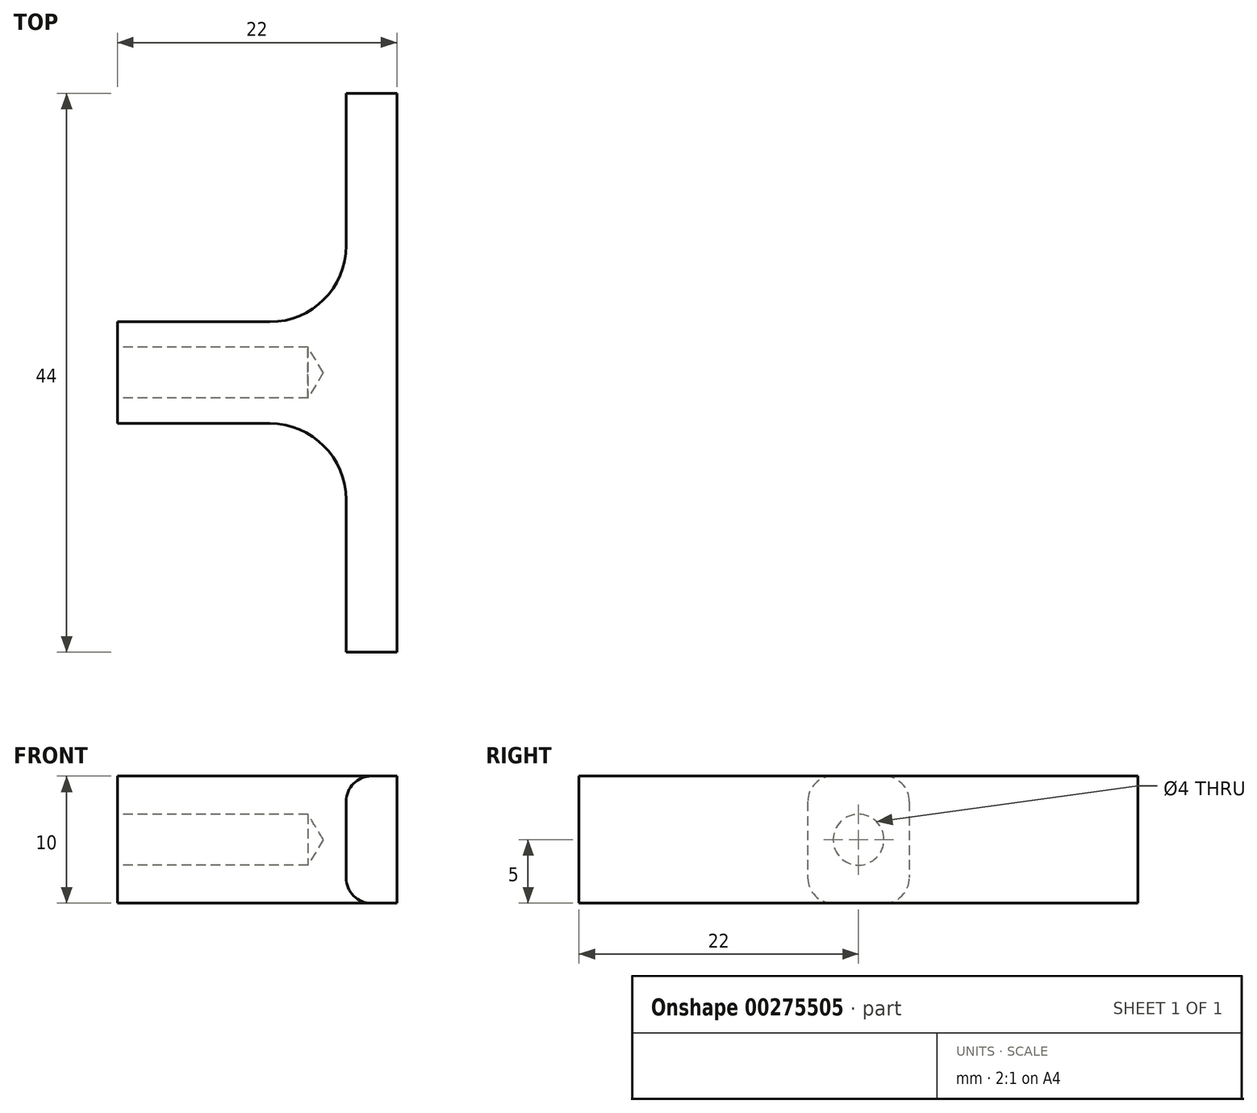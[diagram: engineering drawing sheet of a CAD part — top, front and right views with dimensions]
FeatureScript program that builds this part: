
annotation { "Feature Type Name" : "Feature", "Feature Type Description" : "" }
export const myFeature = defineFeature(function(context is Context, id is Id, definition is map)
    precondition{}
    {
        {
            var Q0;
            Q0=qCreatedBy(makeId("Top.planeOp"),FACE);
            var sketch = newSketch(context, id + "F0", { "sketchPlane" : qUnion([Q0])});
            skLineSegment(sketch, "E0", {"start": v(0, 0) * mm, "end": v(0, -22) * mm});
            skLineSegment(sketch, "E1", {"start": v(0, -22) * mm, "end": v(-4, -22) * mm});
            skLineSegment(sketch, "E2", {"start": v(-4, -22) * mm, "end": v(-4, -10) * mm});
            skLineSegment(sketch, "E3", {"start": v(-10, -4) * mm, "end": v(-22, -4) * mm});
            skLineSegment(sketch, "E4", {"start": v(-22, -4) * mm, "end": v(-22, 0) * mm});
            skPoint(sketch, "E5.visualSharp", {"position": v(-4, -4) * mm});
            skArc(sketch, "E5.filletArc", {"start": v(-4, -10) * mm, "mid": v(-5.76, -5.76) * mm, "end": v(-10, -4) * mm});
            skLineSegment(sketch, "E6.MirrorCS", {"start": v(-22, 4) * mm, "end": v(-22, 0) * mm});
            skLineSegment(sketch, "E7.MirrorCS", {"start": v(-10, 4) * mm, "end": v(-22, 4) * mm});
            skArc(sketch, "E8.MirrorCS", {"start": v(-4, 10) * mm, "mid": v(-5.76, 5.76) * mm, "end": v(-10, 4) * mm});
            skLineSegment(sketch, "E9.MirrorCS", {"start": v(-4, 22) * mm, "end": v(-4, 10) * mm});
            skLineSegment(sketch, "E10.MirrorCS", {"start": v(0, 22) * mm, "end": v(-4, 22) * mm});
            skLineSegment(sketch, "E11.MirrorCS", {"start": v(0, 0) * mm, "end": v(0, 22) * mm});
            skSolve(sketch);
        }
        {
            var Q0;
            Q0=makeQuery(id+"F0.imprint","IMPRINT",FACE,{"disambiguationData":[TD([[makeQuery(id+"F0.imprint","IMPRINT",EDGE,{"derivedFrom":sQuery(id+"F0.wireOp",EDGE,"E0")}),-1.0]])]});
            extrude(context, id + "F1", {"entities" : qUnion([Q0]), "depth" : 10 * mm});
        }
        {
            var Q0;
            Q0=makeQuery(id+"F1.opExtrude","CAP_EDGE",EDGE,{"disambiguationData":[OSD([sQuery(id+"F0.wireOp",EDGE,"E5.filletArc")])],"isStart":false});
            var Q1;
            Q1=makeQuery(id+"F1.opExtrude","CAP_EDGE",EDGE,{"disambiguationData":[OSD([sQuery(id+"F0.wireOp",EDGE,"E9.MirrorCS")])],"isStart":false});
            var Q2;
            Q2=makeQuery(id+"F1.opExtrude","CAP_EDGE",EDGE,{"disambiguationData":[OSD([sQuery(id+"F0.wireOp",EDGE,"E5.filletArc")])],"isStart":true});
            var Q3;
            Q3=makeQuery(id+"F1.opExtrude","CAP_EDGE",EDGE,{"disambiguationData":[OSD([sQuery(id+"F0.wireOp",EDGE,"E8.MirrorCS")])],"isStart":true});
            fillet(context, id + "F2", {"entities" : qUnion([Q0, Q1, Q2, Q3]), "radius" : 2 * mm, "tangentPropagation" : true, "allowEdgeOverflow" : false});
        }
        {
            var Q0;
            Q0=makeQuery(id+"F1.opExtrude","SWEPT_FACE",FACE,{"disambiguationData":[OSD([sQuery(id+"F0.wireOp",EDGE,"E4"),sQuery(id+"F0.wireOp",EDGE,"E6.MirrorCS")])]});
            var sketch = newSketch(context, id + "F3", { "sketchPlane" : qUnion([Q0])});
            skPoint(sketch, "E12", {"position": v(0, 5) * mm});
            skPoint(sketch, "E12.positionSnap0", {"position": v(4, 5) * mm});
            skPoint(sketch, "E12.positionSnap1", {"position": v(0, 10) * mm});
            skSolve(sketch);
        }
        {
            var Q0;
            Q0=sQuery(id+"F3.wireOp",VERTEX,"E12");
            var Q1;
            Q1=makeQuery(id+"F1.opExtrude","SWEPT_BODY",BODY,{"disambiguationData":[OSD([sQuery(id+"F0.wireOp",EDGE,"E0"),sQuery(id+"F0.wireOp",EDGE,"E1"),sQuery(id+"F0.wireOp",EDGE,"E2"),sQuery(id+"F0.wireOp",EDGE,"E3"),sQuery(id+"F0.wireOp",EDGE,"E4"),sQuery(id+"F0.wireOp",EDGE,"E5.filletArc"),sQuery(id+"F0.wireOp",EDGE,"E6.MirrorCS"),sQuery(id+"F0.wireOp",EDGE,"E7.MirrorCS"),sQuery(id+"F0.wireOp",EDGE,"E8.MirrorCS"),sQuery(id+"F0.wireOp",EDGE,"E9.MirrorCS"),sQuery(id+"F0.wireOp",EDGE,"E10.MirrorCS"),sQuery(id+"F0.wireOp",EDGE,"E11.MirrorCS")])]});
            hole(context, id + "F4", {"style" : HoleStyle.SIMPLE, "endStyle" : HoleEndStyle.BLIND, "holeDiameter" : 4 * mm, "holeDepth" : 15 * mm, "tappedDepth" : 12 * mm, "tapClearance" : 3, "locations" : qUnion([Q0]), "scope" : qUnion([Q1])});
        }
    });
